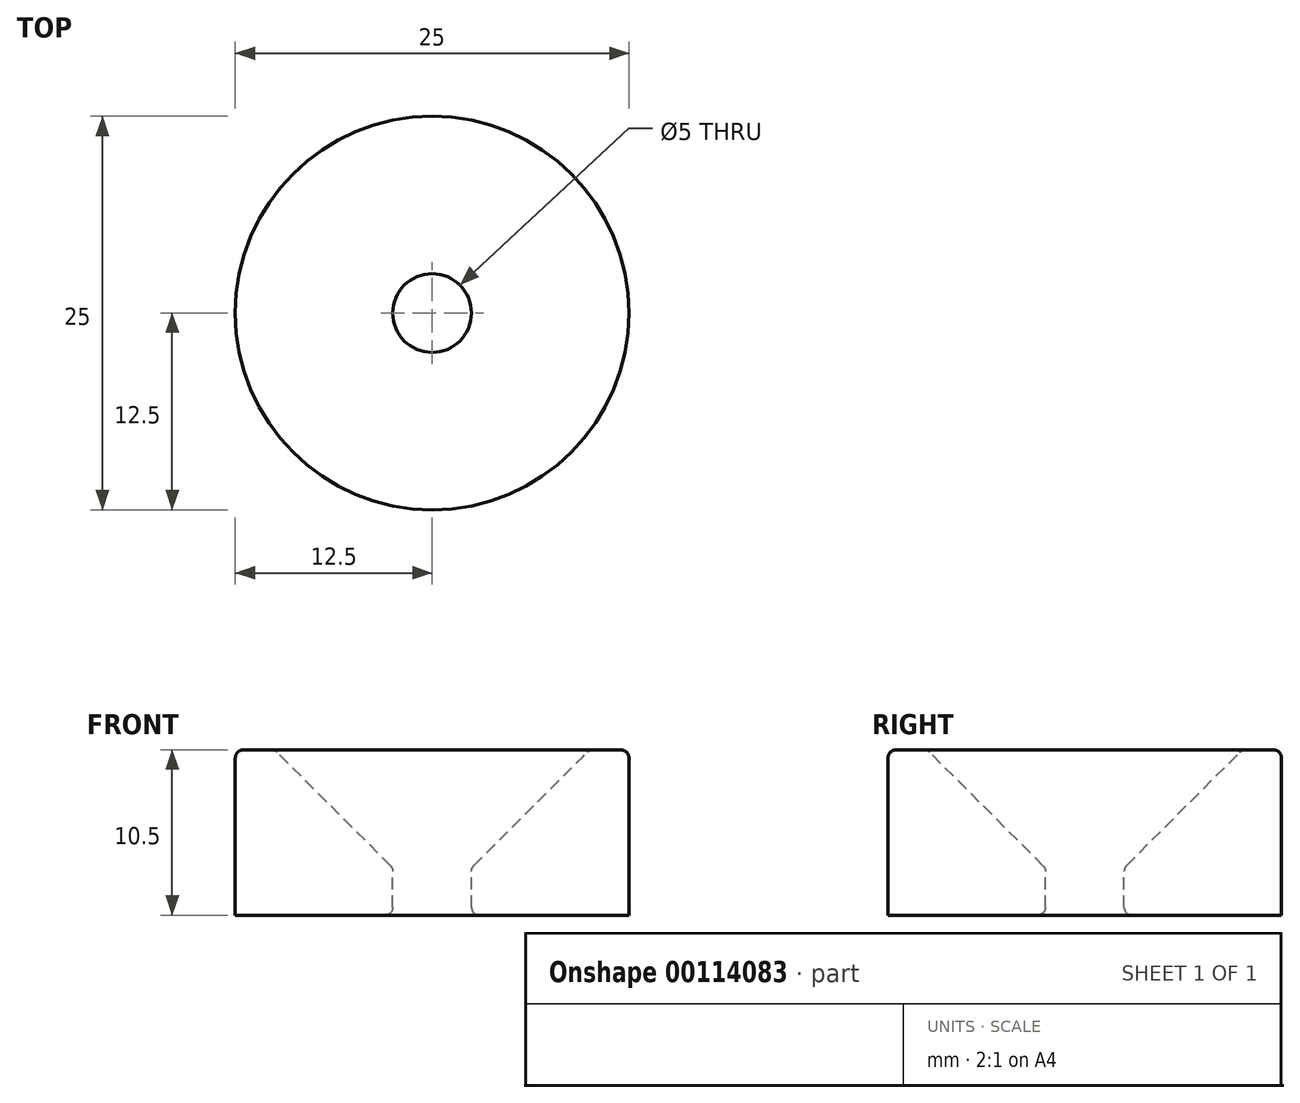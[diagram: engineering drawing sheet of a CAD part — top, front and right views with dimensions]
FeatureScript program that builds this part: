
annotation { "Feature Type Name" : "Feature", "Feature Type Description" : "" }
export const myFeature = defineFeature(function(context is Context, id is Id, definition is map)
    precondition{}
    {
        {
            var Q0;
            Q0=qCreatedBy(makeId("Front.planeOp"),FACE);
            var sketch = newSketch(context, id + "F0", { "sketchPlane" : qUnion([Q0])});
            skLineSegment(sketch, "E0", {"start": v(0, 44.3) * mm, "end": v(0, -13.63) * mm, "construction": true});
            skLineSegment(sketch, "E1", {"start": v(2.5, 3) * mm, "end": v(2.5, 0) * mm});
            skLineSegment(sketch, "E2", {"start": v(2.5, 0) * mm, "end": v(12.5, 0) * mm});
            skLineSegment(sketch, "E3", {"start": v(10, 10.5) * mm, "end": v(12.5, 10.5) * mm});
            skLineSegment(sketch, "E4", {"start": v(12.5, 10.5) * mm, "end": v(12.5, 0) * mm});
            skCircle(sketch, "E5", {"center": v(0, 18.18) * mm, "radius": 12.5 * mm, "construction": true});
            skLineSegment(sketch, "E6", {"start": v(0, 18.18) * mm, "end": v(12.5, 18.18) * mm, "construction": true});
            skLineSegment(sketch, "E7", {"start": v(10, 18.18) * mm, "end": v(10, 10.68) * mm, "construction": true});
            skLineSegment(sketch, "E8", {"start": v(10, 10.68) * mm, "end": v(27.76, 10.68) * mm, "construction": true});
            skLineSegment(sketch, "E9", {"start": v(2.5, 3) * mm, "end": v(10, 10.5) * mm});
            skLineSegment(sketch, "E10", {"start": v(0, 18.18) * mm, "end": v(8.84, 9.34) * mm, "construction": true});
            skSolve(sketch);
        }
        {
            var Q0;
            Q0 = qSketchRegion(id + "F0", true);
            var Q1;
            Q1=sQuery(id+"F0.wireOp",EDGE,"E0");
            revolve(context, id + "F1", {"entities" : qUnion([Q0]), "axis" : qUnion([Q1]), "revolveType" : RevolveType.FULL});
        }
        {
            var Q0;
            Q0=makeQuery(id+"F1.opRevolve","SWEPT_EDGE",EDGE,{"disambiguationData":[OSD([sQuery(id+"F0.wireOp",EDGE,"E3"),sQuery(id+"F0.wireOp",EDGE,"E4")])]});
            var Q1;
            Q1=makeQuery(id+"F1.opRevolve","SWEPT_FACE",FACE,{"disambiguationData":[OSD([sQuery(id+"F0.wireOp",EDGE,"E3")])]});
            var Q2;
            Q2=makeQuery(id+"F1.opRevolve","SWEPT_EDGE",EDGE,{"disambiguationData":[OSD([sQuery(id+"F0.wireOp",EDGE,"E1"),sQuery(id+"F0.wireOp",EDGE,"fUdpSMih-i1vd-xwBk-vJ6x-iyuksEg3VtP9")])]});
            fillet(context, id + "F2", {"entities" : qUnion([Q0, Q1, Q2]), "radius" : 0.5 * mm, "tangentPropagation" : true, "allowEdgeOverflow" : false});
        }
    });
